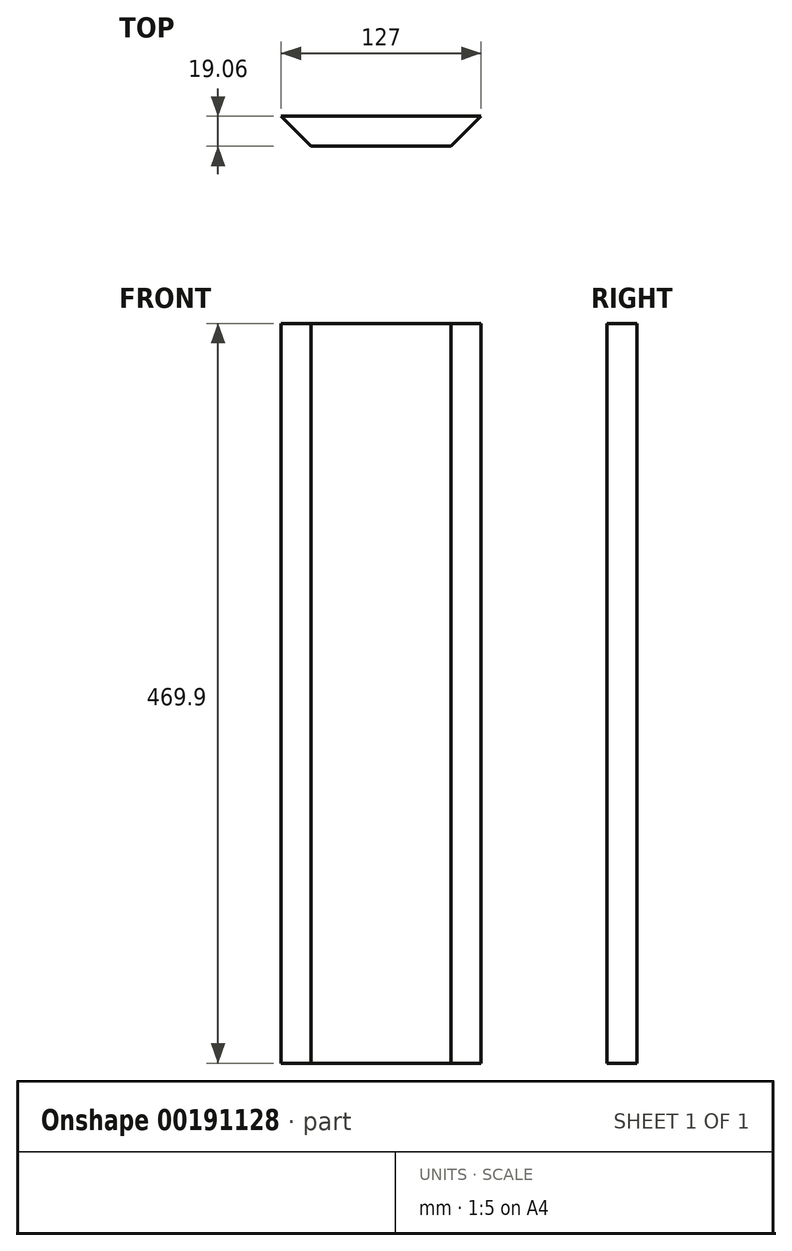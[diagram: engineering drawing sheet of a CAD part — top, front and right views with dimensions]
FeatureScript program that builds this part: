
annotation { "Feature Type Name" : "Feature", "Feature Type Description" : "" }
export const myFeature = defineFeature(function(context is Context, id is Id, definition is map)
    precondition{}
    {
        {
            var Q0;
            Q0=qCreatedBy(makeId("Top.planeOp"),FACE);
            var sketch = newSketch(context, id + "F0", { "sketchPlane" : qUnion([Q0])});
            skLineSegment(sketch, "E0.bottom", {"start": v(38.1, 9.52) * mm, "end": v(-88.9, 9.52) * mm});
            skLineSegment(sketch, "E0.top", {"start": v(19.05, -9.53) * mm, "end": v(-69.85, -9.53) * mm});
            skPoint(sketch, "E0.middle", {"position": v(0, 0) * mm});
            skLineSegment(sketch, "E1", {"start": v(-88.9, 9.52) * mm, "end": v(-69.85, -9.53) * mm});
            skLineSegment(sketch, "E2", {"start": v(38.1, 9.52) * mm, "end": v(19.05, -9.53) * mm});
            skPoint(sketch, "E0.right.end.orphan", {"position": v(-38.1, -9.53) * mm});
            skPoint(sketch, "E0.left.end.orphan", {"position": v(88.9, -9.52) * mm});
            skSolve(sketch);
        }
        {
            var Q0;
            Q0=qSketchRegion(id+"F0",true);
            extrude(context, id + "F1", {"entities" : qUnion([Q0]), "depth" : 469.9 * mm});
        }
    });
